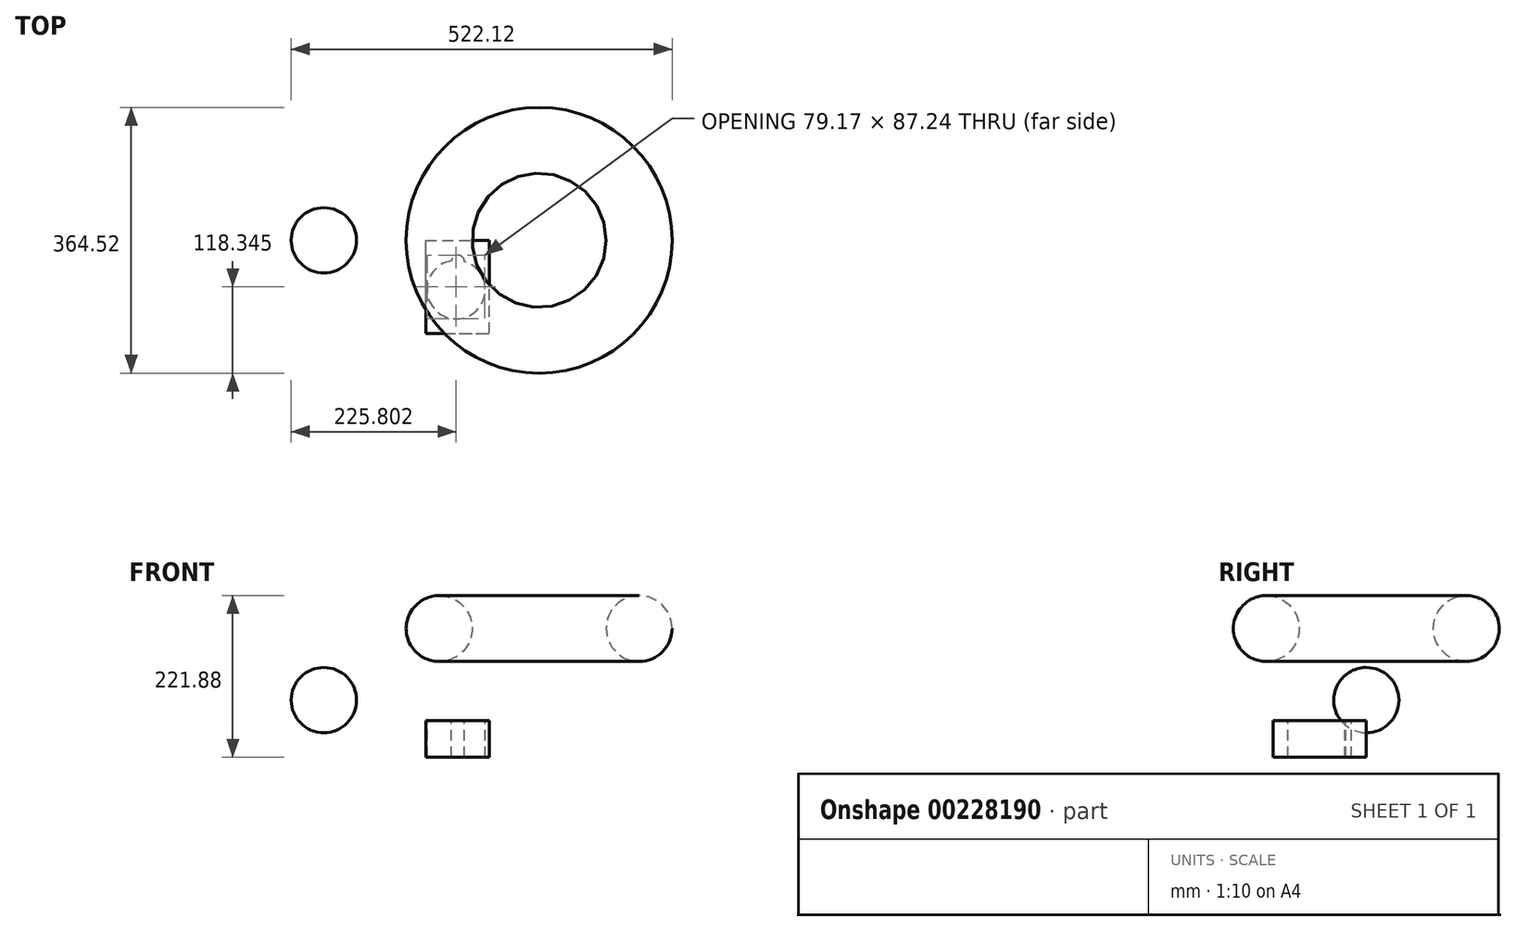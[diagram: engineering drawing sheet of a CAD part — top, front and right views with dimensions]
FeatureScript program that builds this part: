
annotation { "Feature Type Name" : "Feature", "Feature Type Description" : "" }
export const myFeature = defineFeature(function(context is Context, id is Id, definition is map)
    precondition{}
    {
        {
            var Q0;
            Q0=qCreatedBy(makeId("Front.planeOp"),FACE);
            var sketch = newSketch(context, id + "F0", { "sketchPlane" : qUnion([Q0])});
            skLineSegment(sketch, "E0.bottom", {"start": v(0, 0) * mm, "end": v(87.48, 0) * mm});
            skLineSegment(sketch, "E0.top", {"start": v(0, 50.3) * mm, "end": v(87.48, 50.3) * mm});
            skLineSegment(sketch, "E0.left", {"start": v(0, 0) * mm, "end": v(0, 50.3) * mm});
            skLineSegment(sketch, "E0.right", {"start": v(87.48, 0) * mm, "end": v(87.48, 50.3) * mm});
            skSolve(sketch);
        }
        {
            var Q0;
            Q0=makeQuery(id+"F0.imprint","IMPRINT",FACE,{"disambiguationData":[TD([[makeQuery(id+"F0.imprint","IMPRINT",EDGE,{"derivedFrom":sQuery(id+"F0.wireOp",EDGE,"E0.bottom")}),1.0]])]});
            extrude(context, id + "F1", {"entities" : qUnion([Q0]), "depth" : 127.9 * mm});
        }
        {
            var Q0;
            Q0=makeQuery(id+"F1.opExtrude","SWEPT_FACE",FACE,{"disambiguationData":[OSD([sQuery(id+"F0.wireOp",EDGE,"E0.top")])]});
            var sketch = newSketch(context, id + "F2", { "sketchPlane" : qUnion([Q0])});
            skCircle(sketch, "E1", {"center": v(44.13, -29.18) * mm, "radius": 8.9 * mm});
            skCircle(sketch, "E2", {"center": v(41.8, -67.7) * mm, "radius": 39.9 * mm});
            skSolve(sketch);
        }
        {
            var Q0;
            {var subQ0=sQuery(id+"F2.wireOp",EDGE,"E2");var subQ1=sQuery(id+"F2.wireOp",EDGE,"E1");var subQ2=makeQuery(id+"F2.imprint","INTERSECT",VERTEX,{"disambiguationData":[OD(0.0)],"derivedFrom":[subQ1,subQ0]});Q0=makeQuery(id+"F2.imprint","IMPRINT",FACE,{"disambiguationData":[TD([[makeQuery(id+"F2.imprint","IMPRINT",EDGE,{"disambiguationData":[TD([[subQ2,-1.0]])],"derivedFrom":subQ1}),1.0]])]});}
            var Q1;
            {var subQ0=sQuery(id+"F2.wireOp",EDGE,"E2");var subQ1=sQuery(id+"F2.wireOp",EDGE,"E1");var subQ2=makeQuery(id+"F2.imprint","INTERSECT",VERTEX,{"disambiguationData":[OD(0.0)],"derivedFrom":[subQ1,subQ0]});Q1=makeQuery(id+"F2.imprint","IMPRINT",FACE,{"disambiguationData":[TD([[makeQuery(id+"F2.imprint","IMPRINT",EDGE,{"disambiguationData":[TD([[subQ2,1.0]])],"derivedFrom":subQ1}),1.0]])]});}
            var Q2;
            {var subQ0=sQuery(id+"F2.wireOp",EDGE,"E2");var subQ1=sQuery(id+"F2.wireOp",EDGE,"E1");var subQ2=makeQuery(id+"F2.imprint","INTERSECT",VERTEX,{"disambiguationData":[OD(0.0)],"derivedFrom":[subQ1,subQ0]});Q2=makeQuery(id+"F2.imprint","IMPRINT",FACE,{"disambiguationData":[TD([[makeQuery(id+"F2.imprint","IMPRINT",EDGE,{"disambiguationData":[TD([[subQ2,-1.0]])],"derivedFrom":subQ1}),-1.0]])]});}
            extrude(context, id + "F3", {"entities" : qUnion([Q0, Q1, Q2]), "operationType" : NewBodyOperationType.REMOVE, "oppositeDirection" : true, "depth" : 83.7 * mm});
        }
        {
            var Q0;
            Q0=qCreatedBy(makeId("Front.planeOp"),FACE);
            var sketch = newSketch(context, id + "F4", { "sketchPlane" : qUnion([Q0])});
            skLineSegment(sketch, "E3", {"start": v(-139.56, 123.29) * mm, "end": v(-139.56, 33.86) * mm});
            skArc(sketch, "E4", {"start": v(-139.56, 123.29) * mm, "mid": v(-184.27, 78.57) * mm, "end": v(-139.56, 33.86) * mm});
            skPoint(sketch, "E5.orphan", {"position": v(-139.56, 126.8) * mm});
            skPoint(sketch, "E6.orphan", {"position": v(-139.56, 30.34) * mm});
            skSolve(sketch);
        }
        {
            var Q0;
            Q0=makeQuery(id+"F4.imprint","IMPRINT",FACE,{"disambiguationData":[TD([[makeQuery(id+"F4.imprint","IMPRINT",EDGE,{"derivedFrom":sQuery(id+"F4.wireOp",EDGE,"E3")}),-1.0]])]});
            var Q1;
            Q1=sQuery(id+"F4.wireOp",EDGE,"E3");
            revolve(context, id + "F5", {"entities" : qUnion([Q0]), "axis" : qUnion([Q1]), "revolveType" : RevolveType.FULL});
        }
        {
            var Q0;
            Q0=qCreatedBy(makeId("Front.planeOp"),FACE);
            var sketch = newSketch(context, id + "F6", { "sketchPlane" : qUnion([Q0])});
            skCircle(sketch, "E7", {"center": v(18.5, 176.7) * mm, "radius": 45.18 * mm});
            skLineSegment(sketch, "E8", {"start": v(155.59, 244.64) * mm, "end": v(155.59, 76.89) * mm});
            skSolve(sketch);
        }
        {
            var Q0;
            Q0=makeQuery(id+"F6.imprint","IMPRINT",FACE,{"disambiguationData":[TD([[makeQuery(id+"F6.imprint","IMPRINT",EDGE,{"derivedFrom":sQuery(id+"F6.wireOp",EDGE,"E7")}),1.0]])]});
            var Q1;
            Q1=sQuery(id+"F6.wireOp",EDGE,"E8");
            revolve(context, id + "F7", {"entities" : qUnion([Q0]), "axis" : qUnion([Q1]), "revolveType" : RevolveType.FULL});
        }
    });
